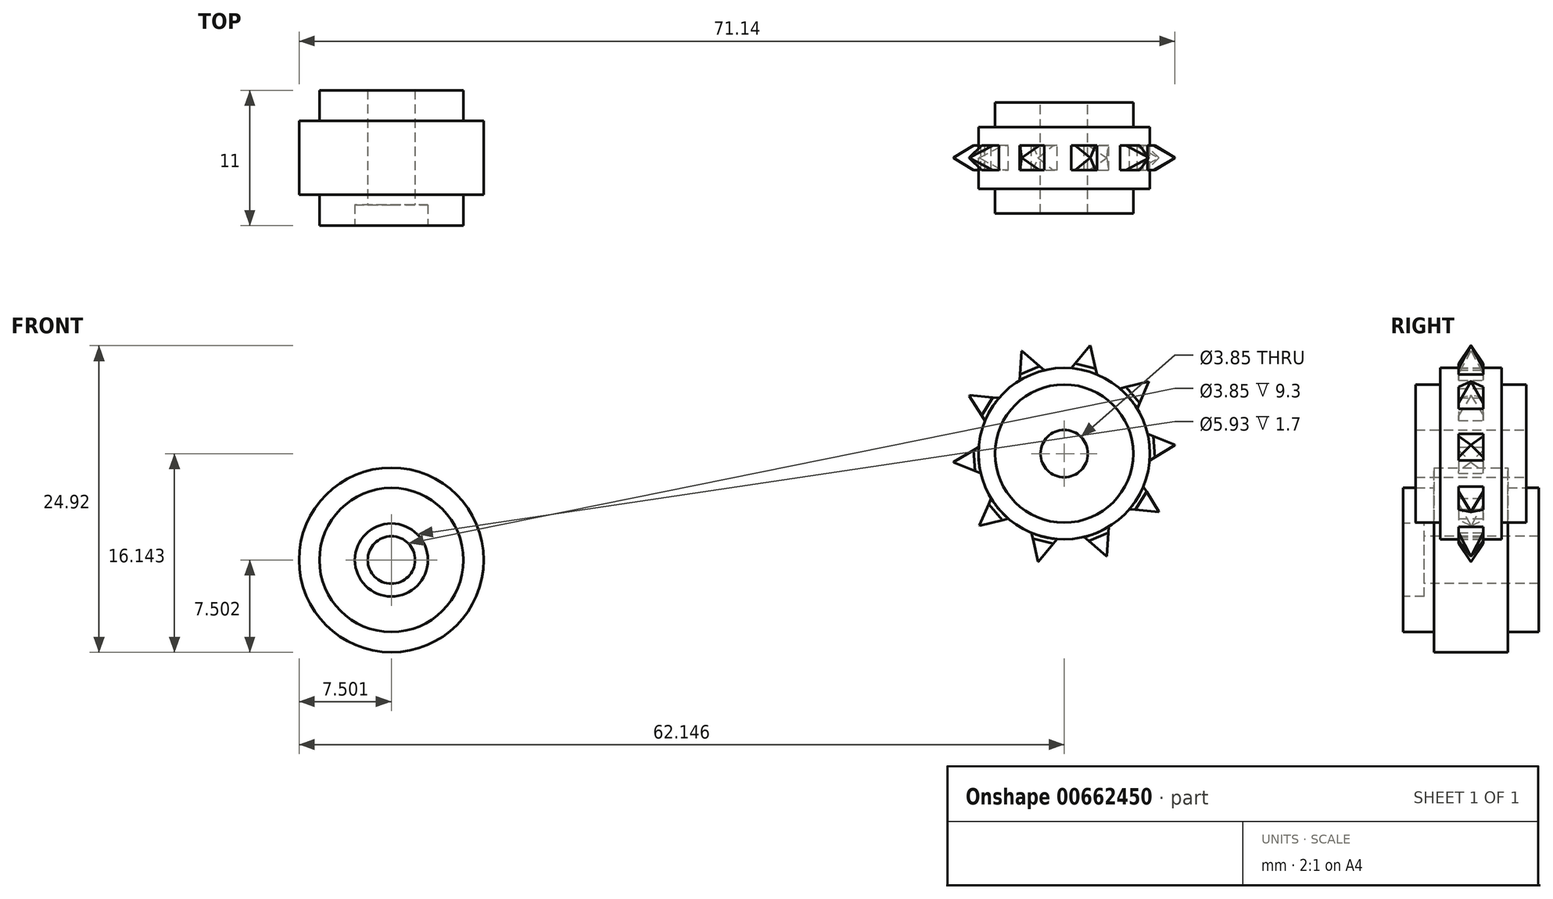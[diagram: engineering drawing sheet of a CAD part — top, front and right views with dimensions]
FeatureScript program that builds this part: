
annotation { "Feature Type Name" : "Feature", "Feature Type Description" : "" }
export const myFeature = defineFeature(function(context is Context, id is Id, definition is map)
    precondition{}
    {
        {
            var Q0;
            Q0=qCreatedBy(makeId("Front.planeOp"),FACE);
            var sketch = newSketch(context, id + "F0", { "sketchPlane" : qUnion([Q0])});
            skCircle(sketch, "E0", {"center": v(-40.43, 7.5) * mm, "radius": 5.85 * mm});
            skCircle(sketch, "E1", {"center": v(-40.43, 7.5) * mm, "radius": 7.5 * mm});
            skSolve(sketch);
        }
        {
            var Q0;
            Q0=makeQuery(id+"F0.imprint","IMPRINT",FACE,{"disambiguationData":[TD([[makeQuery(id+"F0.imprint","IMPRINT",EDGE,{"derivedFrom":sQuery(id+"F0.wireOp",EDGE,"E0")}),1.0]])]});
            extrude(context, id + "F1", {"entities" : qUnion([Q0]), "endBound" : BoundingType.SYMMETRIC, "depth" : 11 * mm, "offsetDistance" : 25 * mm});
        }
        {
            var Q0;
            Q0=makeQuery(id+"F0.imprint","IMPRINT",FACE,{"disambiguationData":[TD([[makeQuery(id+"F0.imprint","IMPRINT",EDGE,{"derivedFrom":sQuery(id+"F0.wireOp",EDGE,"E0")}),-1.0]])]});
            extrude(context, id + "F2", {"entities" : qUnion([Q0]), "operationType" : NewBodyOperationType.ADD, "endBound" : BoundingType.SYMMETRIC, "depth" : 6 * mm, "offsetDistance" : 25 * mm});
        }
        {
            var Q0;
            Q0=makeQuery(id+"F1.opExtrude","CAP_FACE",FACE,{"disambiguationData":[OSD([sQuery(id+"F0.wireOp",EDGE,"E0")])],"isStart":false});
            var sketch = newSketch(context, id + "F3", { "sketchPlane" : qUnion([Q0])});
            skCircle(sketch, "E2.0", {"center": v(-40.43, 7.5) * mm, "radius": 5.85 * mm});
            skCircle(sketch, "E3", {"center": v(-40.43, 7.5) * mm, "radius": 1.92 * mm});
            skCircle(sketch, "E4", {"center": v(-40.43, 7.5) * mm, "radius": 2.96 * mm});
            skSolve(sketch);
        }
        {
            var Q0;
            Q0=makeQuery(id+"F3.imprint","IMPRINT",FACE,{"disambiguationData":[TD([[makeQuery(id+"F3.imprint","IMPRINT",EDGE,{"derivedFrom":sQuery(id+"F3.wireOp",EDGE,"E3")}),1.0]])]});
            extrude(context, id + "F4", {"entities" : qUnion([Q0]), "operationType" : NewBodyOperationType.REMOVE, "oppositeDirection" : true, "depth" : 25 * mm, "offsetDistance" : 25 * mm});
        }
        {
            var Q0;
            Q0=makeQuery(id+"F3.imprint","IMPRINT",FACE,{"disambiguationData":[TD([[makeQuery(id+"F3.imprint","IMPRINT",EDGE,{"derivedFrom":sQuery(id+"F3.wireOp",EDGE,"E3")}),-1.0]])]});
            extrude(context, id + "F5", {"entities" : qUnion([Q0]), "operationType" : NewBodyOperationType.REMOVE, "oppositeDirection" : true, "depth" : 1.7 * mm, "offsetDistance" : 25 * mm});
        }
        {
            var Q0;
            Q0=qCreatedBy(makeId("Front.planeOp"),FACE);
            var sketch = newSketch(context, id + "F6", { "sketchPlane" : qUnion([Q0])});
            skCircle(sketch, "E5.cCircle", {"center": v(14.22, 16.14) * mm, "radius": 9.06 * mm, "construction": true});
            skLineSegment(sketch, "E5.0", {"start": v(21.94, 11.4) * mm, "end": v(17.68, 7.77) * mm});
            skLineSegment(sketch, "E5.1", {"start": v(17.68, 7.77) * mm, "end": v(12.1, 7.33) * mm});
            skLineSegment(sketch, "E5.2", {"start": v(12.1, 7.33) * mm, "end": v(7.32, 10.26) * mm});
            skLineSegment(sketch, "E5.3", {"start": v(7.32, 10.26) * mm, "end": v(5.18, 15.44) * mm});
            skLineSegment(sketch, "E5.4", {"start": v(5.18, 15.44) * mm, "end": v(6.5, 20.88) * mm});
            skLineSegment(sketch, "E5.5", {"start": v(6.5, 20.88) * mm, "end": v(10.75, 24.52) * mm});
            skLineSegment(sketch, "E5.6", {"start": v(10.75, 24.52) * mm, "end": v(16.34, 24.95) * mm});
            skLineSegment(sketch, "E5.7", {"start": v(16.34, 24.95) * mm, "end": v(21.1, 22.02) * mm});
            skLineSegment(sketch, "E5.8", {"start": v(21.1, 22.02) * mm, "end": v(23.25, 16.85) * mm});
            skLineSegment(sketch, "E5.9", {"start": v(23.25, 16.85) * mm, "end": v(21.94, 11.4) * mm});
            skCircle(sketch, "E6", {"center": v(14.22, 16.14) * mm, "radius": 1.92 * mm});
            skLineSegment(sketch, "E7", {"start": v(6.5, 20.88) * mm, "end": v(8.28, 19.78) * mm, "construction": true});
            skLineSegment(sketch, "E8", {"start": v(14.22, 16.14) * mm, "end": v(16.34, 24.95) * mm, "construction": true});
            skPoint(sketch, "E9", {"position": v(10.35, 18.51) * mm});
            skPoint(sketch, "E10", {"position": v(15.28, 20.55) * mm});
            skLineSegment(sketch, "E11", {"start": v(10.35, 18.51) * mm, "end": v(10.49, 20.51) * mm, "construction": true});
            skLineSegment(sketch, "E12", {"start": v(15.28, 20.55) * mm, "end": v(13.77, 21.87) * mm, "construction": true});
            skPoint(sketch, "E13.visualSharp", {"position": v(10.75, 24.52) * mm});
            skLineSegment(sketch, "E14", {"start": v(10.75, 24.47) * mm, "end": v(10.79, 24.49) * mm});
            skLineSegment(sketch, "E15.1.0", {"start": v(9.7, 15.8) * mm, "end": v(8.62, 17.5) * mm, "construction": true});
            skLineSegment(sketch, "E15.1.1", {"start": v(6.52, 20.84) * mm, "end": v(6.54, 20.88) * mm});
            skLineSegment(sketch, "E15.1.2", {"start": v(12.48, 20.33) * mm, "end": v(10.49, 20.51) * mm, "construction": true});
            skLineSegment(sketch, "E15.2.0", {"start": v(10.77, 13.2) * mm, "end": v(8.9, 13.95) * mm, "construction": true});
            skLineSegment(sketch, "E15.2.1", {"start": v(5.23, 15.42) * mm, "end": v(5.22, 15.46) * mm});
            skLineSegment(sketch, "E15.2.2", {"start": v(10.35, 18.51) * mm, "end": v(8.63, 17.49) * mm, "construction": true});
            skLineSegment(sketch, "E15.3.0", {"start": v(13.16, 11.74) * mm, "end": v(11.21, 11.25) * mm, "construction": true});
            skLineSegment(sketch, "E15.3.1", {"start": v(7.37, 10.27) * mm, "end": v(7.34, 10.3) * mm});
            skLineSegment(sketch, "E15.3.2", {"start": v(9.7, 15.8) * mm, "end": v(8.9, 13.95) * mm, "construction": true});
            skLineSegment(sketch, "E15.4.0", {"start": v(15.95, 11.96) * mm, "end": v(14.66, 10.42) * mm, "construction": true});
            skLineSegment(sketch, "E15.4.1", {"start": v(12.12, 7.37) * mm, "end": v(12.09, 7.38) * mm});
            skLineSegment(sketch, "E15.4.2", {"start": v(10.77, 13.2) * mm, "end": v(11.21, 11.25) * mm, "construction": true});
            skLineSegment(sketch, "E15.5.0", {"start": v(18.08, 13.77) * mm, "end": v(17.94, 11.77) * mm, "construction": true});
            skLineSegment(sketch, "E15.5.1", {"start": v(17.68, 7.82) * mm, "end": v(17.64, 7.8) * mm});
            skLineSegment(sketch, "E15.5.2", {"start": v(13.16, 11.74) * mm, "end": v(14.65, 10.43) * mm, "construction": true});
            skLineSegment(sketch, "E15.6.0", {"start": v(18.73, 16.5) * mm, "end": v(19.8, 14.8) * mm, "construction": true});
            skLineSegment(sketch, "E15.6.1", {"start": v(21.91, 11.44) * mm, "end": v(21.9, 11.4) * mm});
            skLineSegment(sketch, "E15.6.2", {"start": v(15.95, 11.96) * mm, "end": v(17.94, 11.77) * mm, "construction": true});
            skLineSegment(sketch, "E15.7.0", {"start": v(17.66, 19.08) * mm, "end": v(19.52, 18.34) * mm, "construction": true});
            skLineSegment(sketch, "E15.7.1", {"start": v(23.2, 16.87) * mm, "end": v(23.2, 16.83) * mm});
            skLineSegment(sketch, "E15.7.2", {"start": v(18.08, 13.77) * mm, "end": v(19.8, 14.8) * mm, "construction": true});
            skLineSegment(sketch, "E15.8.0", {"start": v(15.28, 20.55) * mm, "end": v(17.22, 21.04) * mm, "construction": true});
            skLineSegment(sketch, "E15.8.1", {"start": v(21.06, 22.01) * mm, "end": v(21.1, 21.98) * mm});
            skLineSegment(sketch, "E15.8.2", {"start": v(18.73, 16.5) * mm, "end": v(19.52, 18.34) * mm, "construction": true});
            skLineSegment(sketch, "E15.9.0", {"start": v(12.48, 20.33) * mm, "end": v(13.77, 21.87) * mm, "construction": true});
            skLineSegment(sketch, "E15.9.1", {"start": v(16.3, 24.92) * mm, "end": v(16.35, 24.9) * mm});
            skLineSegment(sketch, "E15.9.2", {"start": v(17.66, 19.08) * mm, "end": v(17.22, 21.04) * mm, "construction": true});
            skLineSegment(sketch, "E16", {"start": v(8.63, 17.49) * mm, "end": v(5.22, 15.46) * mm});
            skLineSegment(sketch, "E17", {"start": v(8.62, 17.5) * mm, "end": v(6.52, 20.84) * mm});
            skLineSegment(sketch, "E18", {"start": v(10.49, 20.51) * mm, "end": v(10.75, 24.47) * mm});
            skLineSegment(sketch, "E19", {"start": v(13.77, 21.87) * mm, "end": v(10.79, 24.49) * mm});
            skLineSegment(sketch, "E20", {"start": v(17.22, 21.04) * mm, "end": v(16.35, 24.9) * mm});
            skLineSegment(sketch, "E21", {"start": v(19.52, 18.34) * mm, "end": v(23.2, 16.87) * mm});
            skLineSegment(sketch, "E22", {"start": v(19.8, 14.8) * mm, "end": v(21.91, 11.44) * mm});
            skLineSegment(sketch, "E23", {"start": v(17.94, 11.77) * mm, "end": v(17.68, 7.82) * mm});
            skLineSegment(sketch, "E24", {"start": v(14.65, 10.43) * mm, "end": v(17.64, 7.8) * mm});
            skLineSegment(sketch, "E25", {"start": v(11.21, 11.25) * mm, "end": v(7.37, 10.27) * mm});
            skLineSegment(sketch, "E26", {"start": v(8.9, 13.95) * mm, "end": v(7.34, 10.3) * mm});
            skLineSegment(sketch, "E27", {"start": v(10.49, 20.51) * mm, "end": v(6.54, 20.88) * mm});
            skLineSegment(sketch, "E28", {"start": v(13.77, 21.87) * mm, "end": v(16.3, 24.92) * mm});
            skLineSegment(sketch, "E29", {"start": v(8.9, 13.95) * mm, "end": v(5.23, 15.42) * mm});
            skLineSegment(sketch, "E30", {"start": v(17.22, 21.04) * mm, "end": v(21.06, 22.01) * mm});
            skLineSegment(sketch, "E31", {"start": v(19.52, 18.34) * mm, "end": v(21.1, 21.98) * mm});
            skLineSegment(sketch, "E32", {"start": v(19.8, 14.8) * mm, "end": v(23.2, 16.83) * mm});
            skLineSegment(sketch, "E33", {"start": v(17.94, 11.77) * mm, "end": v(21.9, 11.4) * mm});
            skLineSegment(sketch, "E34", {"start": v(14.66, 10.42) * mm, "end": v(12.12, 7.37) * mm});
            skLineSegment(sketch, "E35", {"start": v(11.21, 11.25) * mm, "end": v(12.09, 7.38) * mm});
            skCircle(sketch, "E36", {"center": v(14.22, 16.14) * mm, "radius": 6.96 * mm});
            skLineSegment(sketch, "E37", {"start": v(8.28, 19.78) * mm, "end": v(14.22, 16.14) * mm, "construction": true});
            skCircle(sketch, "E38", {"center": v(14.22, 16.14) * mm, "radius": 5.61 * mm});
            skSolve(sketch);
        }
        {
            var Q0;
            Q0=makeQuery(id+"F6.imprint","IMPRINT",FACE,{"disambiguationData":[TD([[makeQuery(id+"F6.imprint","IMPRINT",EDGE,{"derivedFrom":sQuery(id+"F6.wireOp",EDGE,"E6")}),-1.0]])]});
            var Q1;
            Q1=makeQuery(id+"F6.imprint","IMPRINT",FACE,{"disambiguationData":[TD([[makeQuery(id+"F6.imprint","IMPRINT",EDGE,{"derivedFrom":sQuery(id+"F6.wireOp",EDGE,"E38")}),-1.0]])]});
            var Q2;
            {var subQ0=sQuery(id+"F6.wireOp",EDGE,"E29");var subQ1=sQuery(id+"F6.wireOp",EDGE,"E26");var subQ2=makeQuery(id+"F6.imprint","INTERSECT",VERTEX,{"derivedFrom":[subQ1,subQ0]});Q2=makeQuery(id+"F6.imprint","IMPRINT",FACE,{"disambiguationData":[TD([[makeQuery(id+"F6.imprint","IMPRINT",EDGE,{"disambiguationData":[TD([[subQ2,-1.0]])],"derivedFrom":subQ1}),-1.0]])]});}
            var Q3;
            {var subQ0=sQuery(id+"F6.wireOp",EDGE,"E27");var subQ1=sQuery(id+"F6.wireOp",EDGE,"E18");var subQ2=makeQuery(id+"F6.imprint","INTERSECT",VERTEX,{"derivedFrom":[subQ1,subQ0]});Q3=makeQuery(id+"F6.imprint","IMPRINT",FACE,{"disambiguationData":[TD([[makeQuery(id+"F6.imprint","IMPRINT",EDGE,{"disambiguationData":[TD([[subQ2,-1.0]])],"derivedFrom":subQ1}),1.0]])]});}
            var Q4;
            {var subQ0=sQuery(id+"F6.wireOp",EDGE,"E28");var subQ1=sQuery(id+"F6.wireOp",EDGE,"E19");var subQ2=makeQuery(id+"F6.imprint","INTERSECT",VERTEX,{"derivedFrom":[subQ1,subQ0]});Q4=makeQuery(id+"F6.imprint","IMPRINT",FACE,{"disambiguationData":[TD([[makeQuery(id+"F6.imprint","IMPRINT",EDGE,{"disambiguationData":[TD([[subQ2,-1.0]])],"derivedFrom":subQ1}),-1.0]])]});}
            var Q5;
            {var subQ0=sQuery(id+"F6.wireOp",EDGE,"E30");var subQ1=sQuery(id+"F6.wireOp",EDGE,"E20");var subQ2=makeQuery(id+"F6.imprint","INTERSECT",VERTEX,{"derivedFrom":[subQ1,subQ0]});Q5=makeQuery(id+"F6.imprint","IMPRINT",FACE,{"disambiguationData":[TD([[makeQuery(id+"F6.imprint","IMPRINT",EDGE,{"disambiguationData":[TD([[subQ2,-1.0]])],"derivedFrom":subQ1}),-1.0]])]});}
            var Q6;
            {var subQ0=sQuery(id+"F6.wireOp",EDGE,"E31");var subQ1=sQuery(id+"F6.wireOp",EDGE,"E21");var subQ2=makeQuery(id+"F6.imprint","INTERSECT",VERTEX,{"derivedFrom":[subQ1,subQ0]});Q6=makeQuery(id+"F6.imprint","IMPRINT",FACE,{"disambiguationData":[TD([[makeQuery(id+"F6.imprint","IMPRINT",EDGE,{"disambiguationData":[TD([[subQ2,-1.0]])],"derivedFrom":subQ1}),1.0]])]});}
            var Q7;
            {var subQ0=sQuery(id+"F6.wireOp",EDGE,"E32");var subQ1=sQuery(id+"F6.wireOp",EDGE,"E22");var subQ2=makeQuery(id+"F6.imprint","INTERSECT",VERTEX,{"derivedFrom":[subQ1,subQ0]});Q7=makeQuery(id+"F6.imprint","IMPRINT",FACE,{"disambiguationData":[TD([[makeQuery(id+"F6.imprint","IMPRINT",EDGE,{"disambiguationData":[TD([[subQ2,-1.0]])],"derivedFrom":subQ1}),1.0]])]});}
            var Q8;
            {var subQ0=sQuery(id+"F6.wireOp",EDGE,"E33");var subQ1=sQuery(id+"F6.wireOp",EDGE,"E23");var subQ2=makeQuery(id+"F6.imprint","INTERSECT",VERTEX,{"derivedFrom":[subQ1,subQ0]});Q8=makeQuery(id+"F6.imprint","IMPRINT",FACE,{"disambiguationData":[TD([[makeQuery(id+"F6.imprint","IMPRINT",EDGE,{"disambiguationData":[TD([[subQ2,-1.0]])],"derivedFrom":subQ1}),1.0]])]});}
            var Q9;
            {var subQ0=sQuery(id+"F6.wireOp",EDGE,"E34");var subQ1=sQuery(id+"F6.wireOp",EDGE,"E24");var subQ2=makeQuery(id+"F6.imprint","INTERSECT",VERTEX,{"derivedFrom":[subQ1,subQ0]});Q9=makeQuery(id+"F6.imprint","IMPRINT",FACE,{"disambiguationData":[TD([[makeQuery(id+"F6.imprint","IMPRINT",EDGE,{"disambiguationData":[TD([[subQ2,-1.0]])],"derivedFrom":subQ1}),-1.0]])]});}
            var Q10;
            {var subQ0=sQuery(id+"F6.wireOp",EDGE,"E35");var subQ1=sQuery(id+"F6.wireOp",EDGE,"E25");var subQ2=makeQuery(id+"F6.imprint","INTERSECT",VERTEX,{"derivedFrom":[subQ1,subQ0]});Q10=makeQuery(id+"F6.imprint","IMPRINT",FACE,{"disambiguationData":[TD([[makeQuery(id+"F6.imprint","IMPRINT",EDGE,{"disambiguationData":[TD([[subQ2,-1.0]])],"derivedFrom":subQ1}),1.0]])]});}
            extrude(context, id + "F7", {"entities" : qUnion([Q0, Q1, Q2, Q3, Q4, Q5, Q6, Q7, Q8, Q9, Q10]), "endBound" : BoundingType.SYMMETRIC, "depth" : 5 * mm, "offsetDistance" : 25 * mm});
        }
        {
            var Q0;
            {var subQ0=sQuery(id+"F6.wireOp",EDGE,"E15.2.1");Q0=makeQuery(id+"F6.imprint","IMPRINT",FACE,{"disambiguationData":[TD([[makeQuery(id+"F6.imprint","IMPRINT",EDGE,{"derivedFrom":subQ0}),-1.0]])]});}
            var Q1;
            {var subQ0=sQuery(id+"F6.wireOp",EDGE,"E15.1.1");Q1=makeQuery(id+"F6.imprint","IMPRINT",FACE,{"disambiguationData":[TD([[makeQuery(id+"F6.imprint","IMPRINT",EDGE,{"derivedFrom":subQ0}),-1.0]])]});}
            var Q2;
            {var subQ0=sQuery(id+"F6.wireOp",EDGE,"E15.3.1");Q2=makeQuery(id+"F6.imprint","IMPRINT",FACE,{"disambiguationData":[TD([[makeQuery(id+"F6.imprint","IMPRINT",EDGE,{"derivedFrom":subQ0}),-1.0]])]});}
            var Q3;
            {var subQ0=sQuery(id+"F6.wireOp",EDGE,"E15.4.1");Q3=makeQuery(id+"F6.imprint","IMPRINT",FACE,{"disambiguationData":[TD([[makeQuery(id+"F6.imprint","IMPRINT",EDGE,{"derivedFrom":subQ0}),-1.0]])]});}
            var Q4;
            {var subQ0=sQuery(id+"F6.wireOp",EDGE,"E15.5.1");Q4=makeQuery(id+"F6.imprint","IMPRINT",FACE,{"disambiguationData":[TD([[makeQuery(id+"F6.imprint","IMPRINT",EDGE,{"derivedFrom":subQ0}),-1.0]])]});}
            var Q5;
            {var subQ0=sQuery(id+"F6.wireOp",EDGE,"E15.6.1");Q5=makeQuery(id+"F6.imprint","IMPRINT",FACE,{"disambiguationData":[TD([[makeQuery(id+"F6.imprint","IMPRINT",EDGE,{"derivedFrom":subQ0}),-1.0]])]});}
            var Q6;
            {var subQ0=sQuery(id+"F6.wireOp",EDGE,"E15.7.1");Q6=makeQuery(id+"F6.imprint","IMPRINT",FACE,{"disambiguationData":[TD([[makeQuery(id+"F6.imprint","IMPRINT",EDGE,{"derivedFrom":subQ0}),-1.0]])]});}
            var Q7;
            {var subQ0=sQuery(id+"F6.wireOp",EDGE,"E15.8.1");Q7=makeQuery(id+"F6.imprint","IMPRINT",FACE,{"disambiguationData":[TD([[makeQuery(id+"F6.imprint","IMPRINT",EDGE,{"derivedFrom":subQ0}),-1.0]])]});}
            var Q8;
            {var subQ0=sQuery(id+"F6.wireOp",EDGE,"E15.9.1");Q8=makeQuery(id+"F6.imprint","IMPRINT",FACE,{"disambiguationData":[TD([[makeQuery(id+"F6.imprint","IMPRINT",EDGE,{"derivedFrom":subQ0}),-1.0]])]});}
            var Q9;
            {var subQ0=sQuery(id+"F6.wireOp",EDGE,"E14");Q9=makeQuery(id+"F6.imprint","IMPRINT",FACE,{"disambiguationData":[TD([[makeQuery(id+"F6.imprint","IMPRINT",EDGE,{"derivedFrom":subQ0}),-1.0]])]});}
            extrude(context, id + "F8", {"entities" : qUnion([Q0, Q1, Q2, Q3, Q4, Q5, Q6, Q7, Q8, Q9]), "operationType" : NewBodyOperationType.ADD, "endBound" : BoundingType.SYMMETRIC, "depth" : 2 * mm, "offsetDistance" : 25 * mm});
        }
        {
            var Q0;
            Q0=makeQuery(id+"F6.imprint","IMPRINT",FACE,{"disambiguationData":[TD([[makeQuery(id+"F6.imprint","IMPRINT",EDGE,{"derivedFrom":sQuery(id+"F6.wireOp",EDGE,"E6")}),-1.0]])]});
            extrude(context, id + "F9", {"entities" : qUnion([Q0]), "operationType" : NewBodyOperationType.ADD, "endBound" : BoundingType.SYMMETRIC, "depth" : 9 * mm, "offsetDistance" : 25 * mm});
        }
        {
            var Q0;
            Q0=makeQuery(id+"F8.opExtrude","CAP_EDGE",EDGE,{"disambiguationData":[OSD([sQuery(id+"F6.wireOp",EDGE,"E15.6.1")])],"isStart":false});
            var Q1;
            Q1=makeQuery(id+"F8.opExtrude","CAP_EDGE",EDGE,{"disambiguationData":[OSD([sQuery(id+"F6.wireOp",EDGE,"E15.5.1")])],"isStart":false});
            var Q2;
            Q2=makeQuery(id+"F8.opExtrude","CAP_EDGE",EDGE,{"disambiguationData":[OSD([sQuery(id+"F6.wireOp",EDGE,"E15.4.1")])],"isStart":false});
            var Q3;
            Q3=makeQuery(id+"F8.opExtrude","CAP_EDGE",EDGE,{"disambiguationData":[OSD([sQuery(id+"F6.wireOp",EDGE,"E15.3.1")])],"isStart":false});
            var Q4;
            Q4=makeQuery(id+"F8.opExtrude","CAP_EDGE",EDGE,{"disambiguationData":[OSD([sQuery(id+"F6.wireOp",EDGE,"E15.2.1")])],"isStart":false});
            var Q5;
            Q5=makeQuery(id+"F8.opExtrude","CAP_EDGE",EDGE,{"disambiguationData":[OSD([sQuery(id+"F6.wireOp",EDGE,"E15.1.1")])],"isStart":false});
            var Q6;
            Q6=makeQuery(id+"F8.opExtrude","CAP_EDGE",EDGE,{"disambiguationData":[OSD([sQuery(id+"F6.wireOp",EDGE,"E14")])],"isStart":false});
            var Q7;
            Q7=makeQuery(id+"F8.opExtrude","CAP_EDGE",EDGE,{"disambiguationData":[OSD([sQuery(id+"F6.wireOp",EDGE,"E15.9.1")])],"isStart":false});
            var Q8;
            Q8=makeQuery(id+"F8.opExtrude","CAP_EDGE",EDGE,{"disambiguationData":[OSD([sQuery(id+"F6.wireOp",EDGE,"E15.8.1")])],"isStart":false});
            var Q9;
            Q9=makeQuery(id+"F8.opExtrude","CAP_EDGE",EDGE,{"disambiguationData":[OSD([sQuery(id+"F6.wireOp",EDGE,"E15.7.1")])],"isStart":false});
            chamfer(context, id + "F10", {"entities" : qUnion([Q0, Q1, Q2, Q3, Q4, Q5, Q6, Q7, Q8, Q9]), "chamferType" : ChamferType.OFFSET_ANGLE, "width" : .98 * mm, "oppositeDirection" : false, "angle" : 60 * degree, "tangentPropagation" : true});
        }
        {
            var Q0;
            Q0=makeQuery(id+"F8.opExtrude","CAP_EDGE",EDGE,{"disambiguationData":[OSD([sQuery(id+"F6.wireOp",EDGE,"E15.6.1")])],"isStart":true});
            var Q1;
            Q1=makeQuery(id+"F8.opExtrude","CAP_EDGE",EDGE,{"disambiguationData":[OSD([sQuery(id+"F6.wireOp",EDGE,"E15.7.1")])],"isStart":true});
            var Q2;
            Q2=makeQuery(id+"F8.opExtrude","CAP_EDGE",EDGE,{"disambiguationData":[OSD([sQuery(id+"F6.wireOp",EDGE,"E15.8.1")])],"isStart":true});
            var Q3;
            Q3=makeQuery(id+"F8.opExtrude","CAP_EDGE",EDGE,{"disambiguationData":[OSD([sQuery(id+"F6.wireOp",EDGE,"E15.9.1")])],"isStart":true});
            var Q4;
            Q4=makeQuery(id+"F8.opExtrude","CAP_EDGE",EDGE,{"disambiguationData":[OSD([sQuery(id+"F6.wireOp",EDGE,"E14")])],"isStart":true});
            var Q5;
            Q5=makeQuery(id+"F8.opExtrude","CAP_EDGE",EDGE,{"disambiguationData":[OSD([sQuery(id+"F6.wireOp",EDGE,"E15.1.1")])],"isStart":true});
            var Q6;
            Q6=makeQuery(id+"F8.opExtrude","CAP_EDGE",EDGE,{"disambiguationData":[OSD([sQuery(id+"F6.wireOp",EDGE,"E15.2.1")])],"isStart":true});
            var Q7;
            Q7=makeQuery(id+"F8.opExtrude","CAP_EDGE",EDGE,{"disambiguationData":[OSD([sQuery(id+"F6.wireOp",EDGE,"E15.3.1")])],"isStart":true});
            var Q8;
            Q8=makeQuery(id+"F8.opExtrude","CAP_EDGE",EDGE,{"disambiguationData":[OSD([sQuery(id+"F6.wireOp",EDGE,"E15.4.1")])],"isStart":true});
            var Q9;
            Q9=makeQuery(id+"F8.opExtrude","CAP_EDGE",EDGE,{"disambiguationData":[OSD([sQuery(id+"F6.wireOp",EDGE,"E15.5.1")])],"isStart":true});
            chamfer(context, id + "F11", {"entities" : qUnion([Q0, Q1, Q2, Q3, Q4, Q5, Q6, Q7, Q8, Q9]), "chamferType" : ChamferType.OFFSET_ANGLE, "width" : 1.7 * mm, "oppositeDirection" : false, "angle" : 30 * degree, "tangentPropagation" : true});
        }
    });
